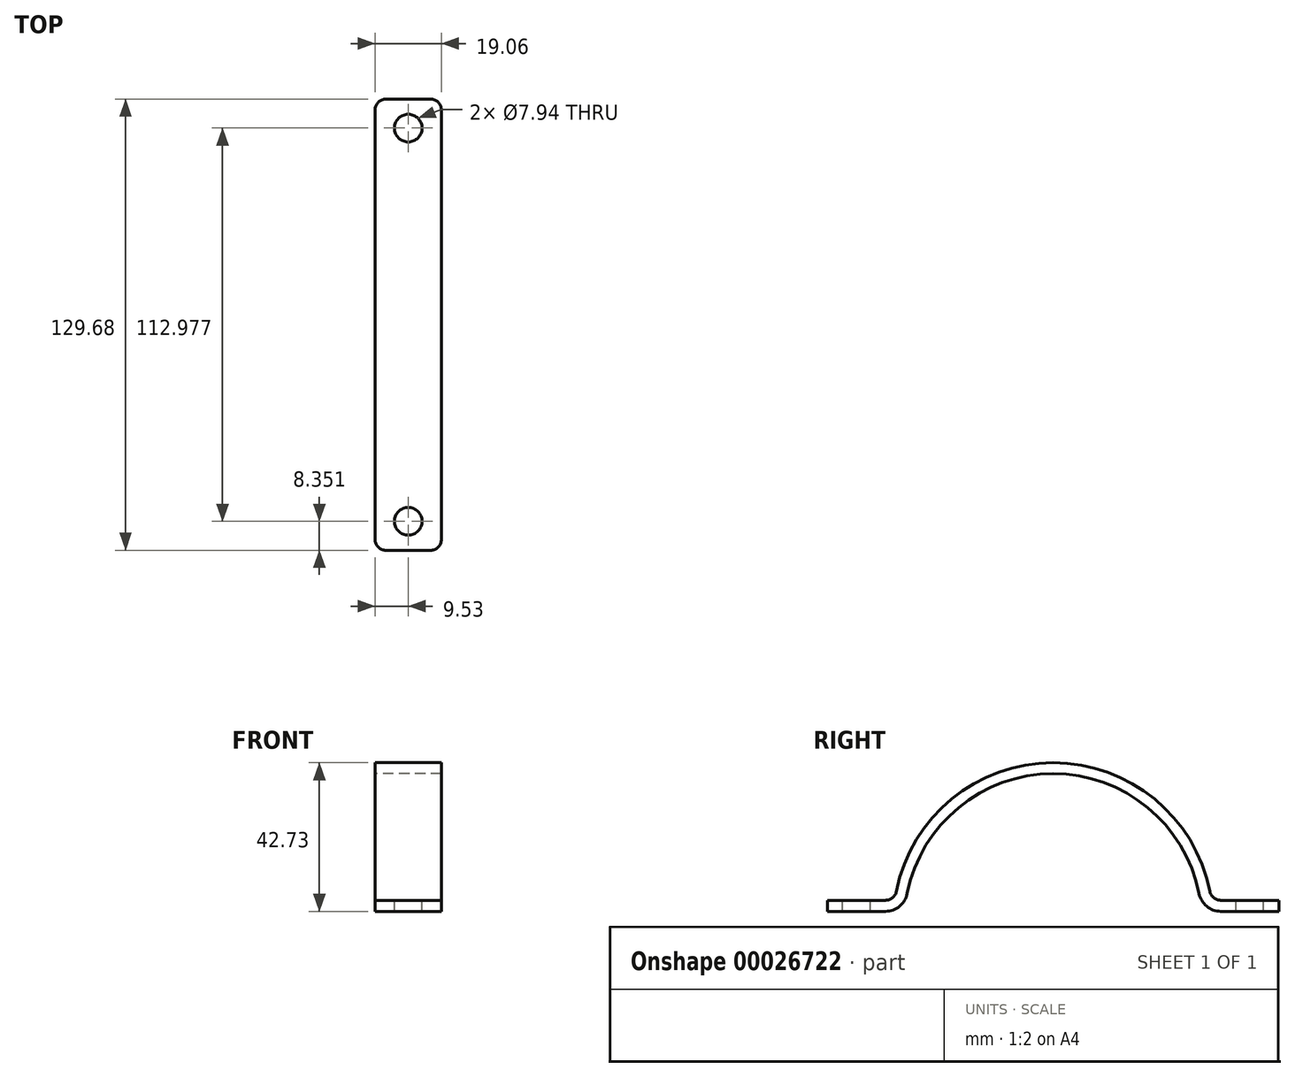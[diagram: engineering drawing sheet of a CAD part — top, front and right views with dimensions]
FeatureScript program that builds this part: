
annotation { "Feature Type Name" : "Feature", "Feature Type Description" : "" }
export const myFeature = defineFeature(function(context is Context, id is Id, definition is map)
    precondition{}
    {
        {
            var Q0;
            Q0=qCreatedBy(makeId("Right.planeOp"),FACE);
            var sketch = newSketch(context, id + "F0", { "sketchPlane" : qUnion([Q0])});
            skArc(sketch, "E0", {"start": v(42.6, 3.17) * mm, "mid": v(0, 42.72) * mm, "end": v(-42.6, 3.17) * mm});
            skArc(sketch, "E1", {"start": v(45.46, 6.35) * mm, "mid": v(0, 45.9) * mm, "end": v(-45.46, 6.35) * mm});
            skLineSegment(sketch, "E2.0", {"start": v(-64.84, 3.18) * mm, "end": v(-42.6, 3.18) * mm});
            skLineSegment(sketch, "E3.0", {"start": v(-64.84, 6.35) * mm, "end": v(-45.46, 6.35) * mm});
            skLineSegment(sketch, "E4", {"start": v(-45.79, 3.18) * mm, "end": v(-45.79, -9.23) * mm});
            skLineSegment(sketch, "E5.0", {"start": v(-64.84, 6.35) * mm, "end": v(-64.84, 3.18) * mm});
            skLineSegment(sketch, "E6", {"start": v(0, 0) * mm, "end": v(0, -29.1) * mm, "construction": true});
            skLineSegment(sketch, "E7.MirrorCS", {"start": v(64.84, 6.35) * mm, "end": v(64.84, 3.18) * mm});
            skLineSegment(sketch, "E8.trimOffspring", {"start": v(45.46, 6.35) * mm, "end": v(64.84, 6.35) * mm});
            skLineSegment(sketch, "E9.trimOffspring", {"start": v(42.6, 3.18) * mm, "end": v(64.84, 3.18) * mm});
            skSolve(sketch);
        }
        {
            var Q0;
            Q0 = qSketchRegion(id + "F0", true);
            extrude(context, id + "F1", {"entities" : qUnion([Q0]), "endBound" : BoundingType.SYMMETRIC, "depth" : 19.05 * mm});
        }
        {
            var Q0;
            Q0=makeQuery(id+"F1.opExtrude","SWEPT_EDGE",EDGE,{"disambiguationData":[OSD([sQuery(id+"F0.wireOp",EDGE,"E1"),sQuery(id+"F0.wireOp",EDGE,"E8.trimOffspring")])]});
            var Q1;
            Q1=makeQuery(id+"F1.opExtrude","SWEPT_EDGE",EDGE,{"disambiguationData":[OSD([sQuery(id+"F0.wireOp",EDGE,"E1"),sQuery(id+"F0.wireOp",EDGE,"E3.0")])]});
            fillet(context, id + "F2", {"entities" : qUnion([Q0, Q1]), "radius" : 3.17 * mm, "tangentPropagation" : true, "allowEdgeOverflow" : false});
        }
        {
            var Q0;
            Q0=makeQuery(id+"F1.opExtrude","SWEPT_EDGE",EDGE,{"disambiguationData":[OSD([sQuery(id+"F0.wireOp",EDGE,"E0"),sQuery(id+"F0.wireOp",EDGE,"E2.0")])]});
            var Q1;
            Q1=makeQuery(id+"F1.opExtrude","SWEPT_EDGE",EDGE,{"disambiguationData":[OSD([sQuery(id+"F0.wireOp",EDGE,"E0"),sQuery(id+"F0.wireOp",EDGE,"E9.trimOffspring")])]});
            fillet(context, id + "F3", {"entities" : qUnion([Q0, Q1]), "radius" : 6.35 * mm, "tangentPropagation" : true, "allowEdgeOverflow" : false});
        }
        {
            var Q0;
            Q0=makeQuery(id+"F1.opExtrude","CAP_EDGE",EDGE,{"disambiguationData":[OSD([sQuery(id+"F0.wireOp",EDGE,"E7.MirrorCS")])],"isStart":false});
            var Q1;
            Q1=makeQuery(id+"F1.opExtrude","CAP_EDGE",EDGE,{"disambiguationData":[OSD([sQuery(id+"F0.wireOp",EDGE,"E7.MirrorCS")])],"isStart":true});
            var Q2;
            Q2=makeQuery(id+"F1.opExtrude","CAP_EDGE",EDGE,{"disambiguationData":[OSD([sQuery(id+"F0.wireOp",EDGE,"E5.0")])],"isStart":false});
            var Q3;
            Q3=makeQuery(id+"F1.opExtrude","CAP_EDGE",EDGE,{"disambiguationData":[OSD([sQuery(id+"F0.wireOp",EDGE,"E5.0")])],"isStart":true});
            fillet(context, id + "F4", {"entities" : qUnion([Q0, Q1, Q2, Q3]), "radius" : 3.17 * mm, "tangentPropagation" : true, "allowEdgeOverflow" : false});
        }
        {
            var Q0;
            Q0=makeQuery(id+"F1.opExtrude","SWEPT_FACE",FACE,{"disambiguationData":[OSD([sQuery(id+"F0.wireOp",EDGE,"E3.0")])]});
            var sketch = newSketch(context, id + "F5", { "sketchPlane" : qUnion([Q0])});
            skLineSegment(sketch, "E10", {"start": v(0, -48.14) * mm, "end": v(0, -64.84) * mm, "construction": true});
            skPoint(sketch, "E11", {"position": v(0, -56.49) * mm});
            skLineSegment(sketch, "E12", {"start": v(0, 0) * mm, "end": v(35.3, 0) * mm, "construction": true});
            skPoint(sketch, "E13.MirrorP", {"position": v(0, 56.49) * mm});
            skSolve(sketch);
        }
        {
            var Q0;
            Q0=sQuery(id+"F5.wireOp",VERTEX,"E11");
            var Q1;
            Q1=sQuery(id+"F5.wireOp",VERTEX,"E13.MirrorP");
            var Q2;
            Q2=makeQuery(id+"F1.opExtrude","SWEPT_BODY",BODY,{"disambiguationData":[OSD([sQuery(id+"F0.wireOp",EDGE,"E0"),sQuery(id+"F0.wireOp",EDGE,"E1"),sQuery(id+"F0.wireOp",EDGE,"E2.0"),sQuery(id+"F0.wireOp",EDGE,"E3.0"),sQuery(id+"F0.wireOp",EDGE,"E5.0"),sQuery(id+"F0.wireOp",EDGE,"E7.MirrorCS"),sQuery(id+"F0.wireOp",EDGE,"E8.trimOffspring"),sQuery(id+"F0.wireOp",EDGE,"E9.trimOffspring")])]});
            hole(context, id + "F6", {"style" : HoleStyle.SIMPLE, "holeDiameter" : 7.94 * mm, "endStyle" : HoleEndStyle.THROUGH, "locations" : qUnion([Q0, Q1]), "scope" : qUnion([Q2])});
        }
    });
